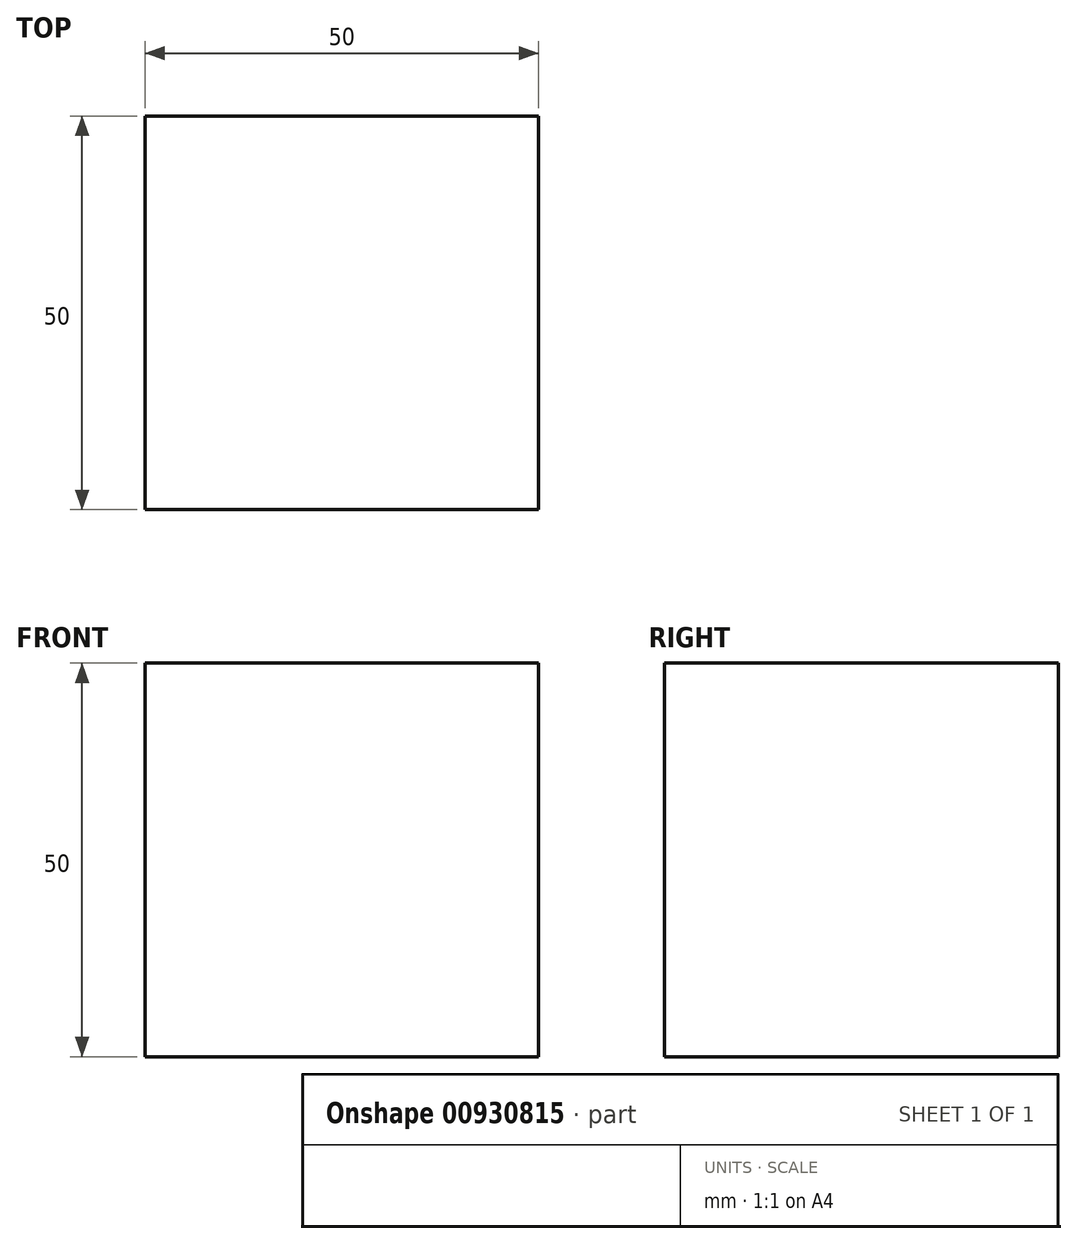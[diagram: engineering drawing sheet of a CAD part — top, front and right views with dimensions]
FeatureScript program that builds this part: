
annotation { "Feature Type Name" : "Feature", "Feature Type Description" : "" }
export const myFeature = defineFeature(function(context is Context, id is Id, definition is map)
    precondition{}
    {
        {
            var Q0;
            Q0=qCreatedBy(makeId("Right.planeOp"),FACE);
            var sketch = newSketch(context, id + "F0", { "sketchPlane" : qUnion([Q0])});
            skLineSegment(sketch, "E0.bottom", {"start": v(0, 0) * mm, "end": v(50, 0) * mm});
            skLineSegment(sketch, "E0.top", {"start": v(0, -50) * mm, "end": v(50, -50) * mm});
            skLineSegment(sketch, "E0.left", {"start": v(0, 0) * mm, "end": v(0, -50) * mm});
            skLineSegment(sketch, "E0.right", {"start": v(50, 0) * mm, "end": v(50, -50) * mm});
            skSolve(sketch);
        }
        {
            var Q0;
            Q0 = qSketchRegion(id + "F0", true);
            extrude(context, id + "F1", {"entities" : qUnion([Q0]), "depth" : 50 * mm, "offsetDistance" : 25 * mm});
        }
    });
